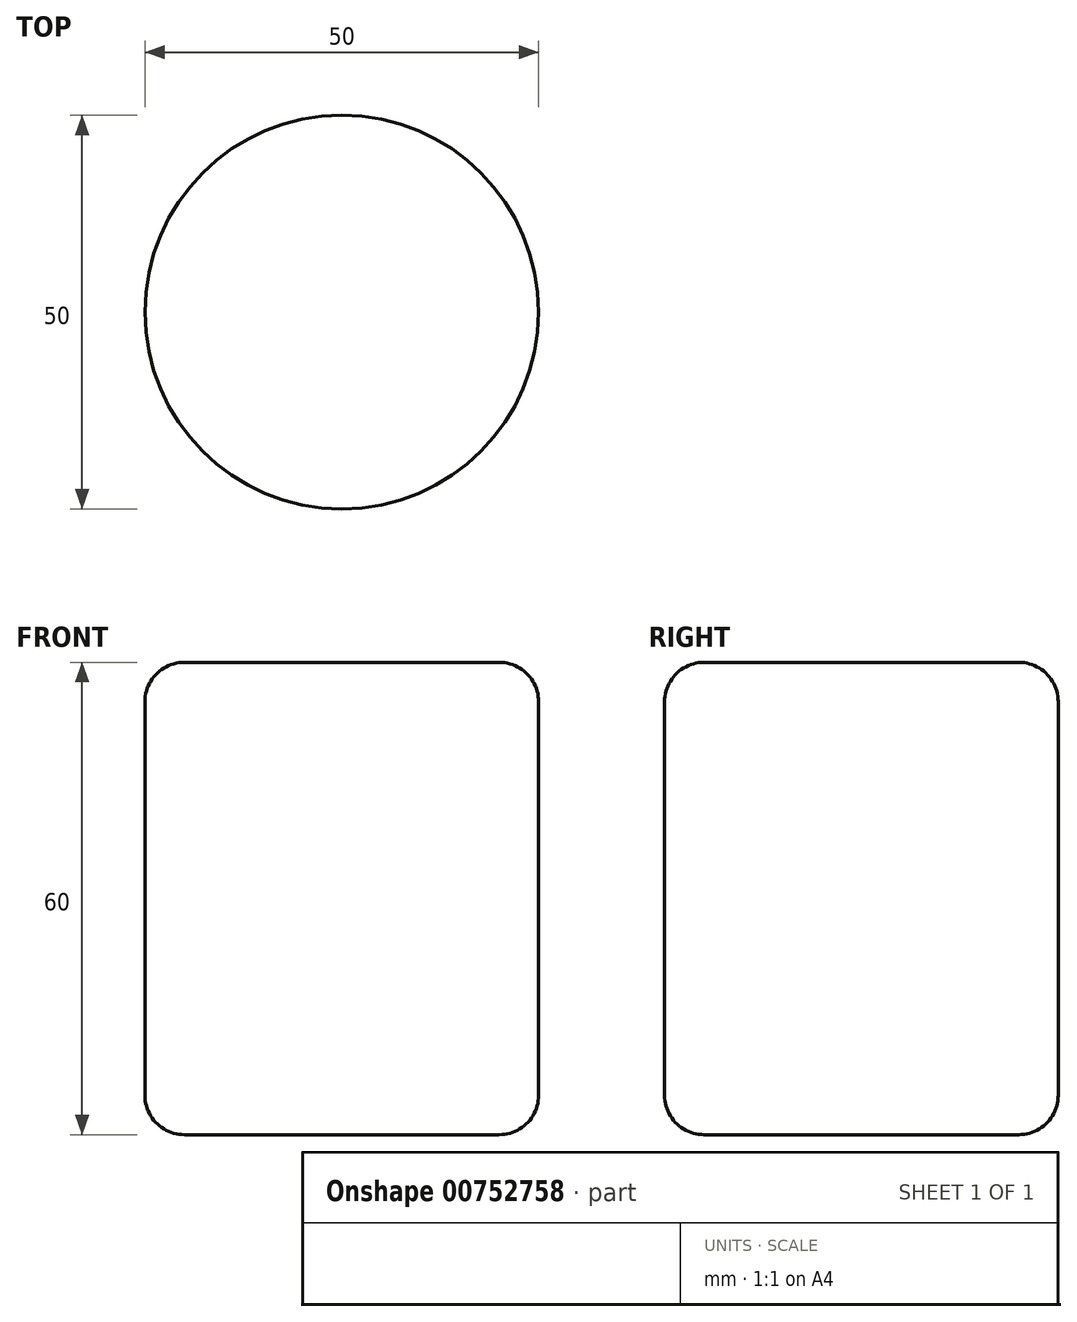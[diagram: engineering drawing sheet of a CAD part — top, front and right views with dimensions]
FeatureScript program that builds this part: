
annotation { "Feature Type Name" : "Feature", "Feature Type Description" : "" }
export const myFeature = defineFeature(function(context is Context, id is Id, definition is map)
    precondition{}
    {
        {
            var Q0;
            Q0=qCreatedBy(makeId("Front.planeOp"),FACE);
            var sketch = newSketch(context, id + "F0", { "sketchPlane" : qUnion([Q0])});
            skLineSegment(sketch, "E0.bottom", {"start": v(0, 0) * mm, "end": v(-25, 0) * mm});
            skLineSegment(sketch, "E0.top", {"start": v(0, 60) * mm, "end": v(-25, 60) * mm});
            skLineSegment(sketch, "E0.left", {"start": v(0, 0) * mm, "end": v(0, 60) * mm});
            skLineSegment(sketch, "E0.right", {"start": v(-25, 0) * mm, "end": v(-25, 60) * mm});
            skSolve(sketch);
        }
        {
            var Q0;
            Q0 = qSketchRegion(id + "F0", true);
            var Q1;
            Q1=sQuery(id+"F0.wireOp",EDGE,"E0.left");
            revolve(context, id + "F1", {"surfaceOperationType" : NewSurfaceOperationType.NEW, "entities" : qUnion([Q0]), "axis" : qUnion([Q1]), "revolveType" : RevolveType.FULL});
        }
        {
            var Q0;
            Q0=makeQuery(id+"F1.opRevolve","SWEPT_EDGE",EDGE,{"disambiguationData":[OSD([sQuery(id+"F0.wireOp",EDGE,"E0.top"),sQuery(id+"F0.wireOp",EDGE,"E0.right")])]});
            var Q1;
            Q1=makeQuery(id+"F1.opRevolve","SWEPT_EDGE",EDGE,{"disambiguationData":[OSD([sQuery(id+"F0.wireOp",EDGE,"E0.bottom"),sQuery(id+"F0.wireOp",EDGE,"E0.right")])]});
            fillet(context, id + "F2", {"entities" : qUnion([Q0, Q1]), "radius" : 5 * mm, "tangentPropagation" : true, "allowEdgeOverflow" : false});
        }
    });
